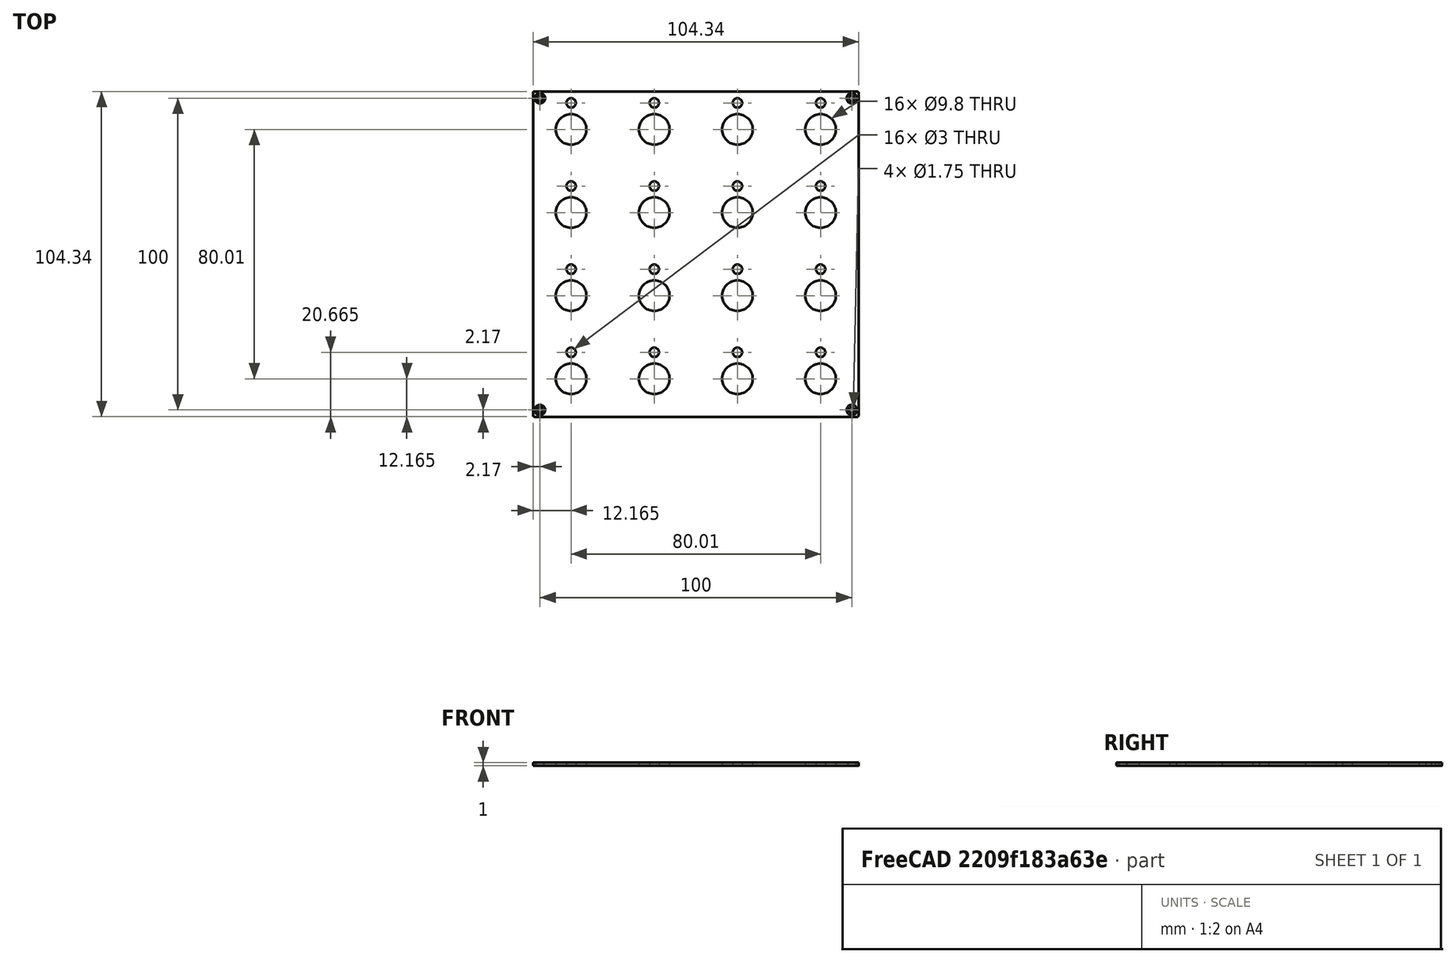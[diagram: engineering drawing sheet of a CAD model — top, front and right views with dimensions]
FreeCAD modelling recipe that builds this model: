
FCSTD DOCUMENT  (FreeCAD 0.21R33771 (Git))
Label: FRONTPANEL-SHEET-BU16
License: All rights reserved
LicenseURL: https://en.wikipedia.org/wiki/All_rights_reserved
objects: TechDraw::DrawViewBalloon×13, TechDraw::DrawViewDimension×8, TechDraw::DrawHatch×7, Sketcher::SketchObject×6, TechDraw::DrawViewPart×5, PartDesign::Hole×3, TechDraw::DrawViewAnnotation×3, TechDraw::DrawSVGTemplate×2, PartDesign::Body×2, TechDraw::DrawPage×2, Spreadsheet::Sheet×1, PartDesign::Pad×1, PartDesign::Pocket×1, PartDesign::FeatureBase×1, TechDraw::DrawComplexSection×1
note: 30 computed .brp shape members not serialized (recipe doc carries the construction recipe); baked Part::Feature solids carry a one-line shape summary decoded from their .brp

FEATURE [TechDraw::DrawSVGTemplate] Template003
  EditableTexts = COLOR=Anodized matte black - RAL code: 9004; CreationDate=2024/05/14; E.G.APPROVED=APPROVED; FC-Scale=1:1; FC-Title=BU16 - frontpanel; IntechStudioLtd.=Intech Studio Ltd.; MATERIAL=Aluminum 5052-H32; REV=03; STANDARD=ISO 2768 - m
  Height = 297
  Orientation = 1
  Template = <userpath>/Desktop/A3_LandscapeTD_MODIFIED.svg
  Width = 420
FEATURE [Spreadsheet::Sheet] Spreadsheet  label="dim"
  cells = A1='panel_length; B1(panel_length)=104.35; A2='panel_thickness; B2(panel_thickness)=1; A3='panel_radius; B3(panel_radius)==(104.35 - 103.6) / 2; A5='corner_drill_dist; B5(corner_drill_dist)=100; A6='corner_drill_dia; B6(corner_drill_dia)=1.75; A7='corner_drill_countersink; B7(corner_drill_countersink)=3.3; A9='undercut_width; B9(undercut_width)=1; A10='undercut_length; B10(undercut_length)=90; A11='undercut_offset; B11(undercut_offset)=1; A12='undercut_depth; B12(undercut_depth)=0.8; A14='ui_raster; B14(ui_raster)=26.67; A16='light_drill_dia; B16(light_drill_dia)=3; D16='old 2.9; A17='light_bore_dia; B17(light_bore_dia)=3.45; C17='check; D17='old 3.30; E17='DEPRICATED; A18='light_bore_depth; B18(light_bore_depth)=0.4; C18='check; D18='old 0.40; E18='DEPRICATED; A20='pot_drill_dia; B20(pot_drill_dia)=9.7; C20='check; D20='old 6.20; A21='pot_led_dist; B21(pot_led_dist)=8.5; B22=0; A23='but_drill_dia; B23(but_drill_dia)=9.8; A24='but_led_dist; B24(but_led_dist)=8.5; A26='fad_cutout_width; B26(fad_cutout_width)=2; C26='check; D26='old 1.50; A27='fad_cutout_length; B27(fad_cutout_length)=36; A28='fad_led_dist; B28(fad_led_dist)=25; A30='enc_drill_dia; B30(enc_drill_dia)=9.7; C30='check; D30='old 6.20; A31='enc_led_dist; B31(enc_led_dist)=8.5; A33='longfad_cutout_width; B33(longfad_cutout_width)=2; A34='longfad_cutout_length; B34(longfad_cutout_length)=66; A36='panel_chamfer; B36(panel_chamfer)=0.2; C36='UPDATE DRAWING
FEATURE [Sketcher::SketchObject] Sketch006
  FullyConstrained = true
  MapMode = 5
  Support = -> [XY_Plane002]
  expr: Constraints[4] = <<dim>>.ui_raster
  expr: Constraints[84] = <<dim>>.but_led_dist
  sketch-geometry (34):
    g0: Circle CenterX=-40.005 CenterY=48.505 CenterZ=0 NormalX=0 NormalY=0 NormalZ=1 AngleXU=0 Radius=2
    g1: Circle CenterX=-13.335 CenterY=48.505 CenterZ=0 NormalX=0 NormalY=0 NormalZ=1 AngleXU=0 Radius=2
    g2: LineSegment StartX=-40.005 StartY=48.505 StartZ=0 EndX=-13.335 EndY=48.505 EndZ=0
    g3: Circle CenterX=13.335 CenterY=48.505 CenterZ=0 NormalX=0 NormalY=0 NormalZ=1 AngleXU=0 Radius=2
    g4: LineSegment StartX=-13.335 StartY=48.505 StartZ=0 EndX=13.335 EndY=48.505 EndZ=0
    g5: Circle CenterX=40.005 CenterY=48.505 CenterZ=0 NormalX=0 NormalY=0 NormalZ=1 AngleXU=0 Radius=2
    g6: LineSegment StartX=13.335 StartY=48.505 StartZ=0 EndX=40.005 EndY=48.505 EndZ=0
    g7: Circle CenterX=-40.005 CenterY=21.835 CenterZ=0 NormalX=0 NormalY=0 NormalZ=1 AngleXU=0 Radius=2
    g8: LineSegment StartX=-40.005 StartY=48.505 StartZ=0 EndX=-40.005 EndY=21.835 EndZ=0
    g9: Circle CenterX=-13.335 CenterY=21.835 CenterZ=0 NormalX=0 NormalY=0 NormalZ=1 AngleXU=0 Radius=2
    g10: LineSegment StartX=-40.005 StartY=21.835 StartZ=0 EndX=-13.335 EndY=21.835 EndZ=0
    g11: Circle CenterX=13.335 CenterY=21.835 CenterZ=0 NormalX=0 NormalY=0 NormalZ=1 AngleXU=0 Radius=2
    g12: LineSegment StartX=-13.335 StartY=21.835 StartZ=0 EndX=13.335 EndY=21.835 EndZ=0
    g13: Circle CenterX=40.005 CenterY=21.835 CenterZ=0 NormalX=0 NormalY=0 NormalZ=1 AngleXU=0 Radius=2
    g14: LineSegment StartX=13.335 StartY=21.835 StartZ=0 EndX=40.005 EndY=21.835 EndZ=0
    g15: Circle CenterX=-40.005 CenterY=-4.835 CenterZ=0 NormalX=0 NormalY=0 NormalZ=1 AngleXU=0 Radius=2
    g16: LineSegment StartX=-40.005 StartY=21.835 StartZ=0 EndX=-40.005 EndY=-4.835 EndZ=0
    g17: Circle CenterX=-13.335 CenterY=-4.835 CenterZ=0 NormalX=0 NormalY=0 NormalZ=1 AngleXU=0 Radius=2
    g18: LineSegment StartX=-40.005 StartY=-4.835 StartZ=0 EndX=-13.335 EndY=-4.835 EndZ=0
    g19: Circle CenterX=13.335 CenterY=-4.835 CenterZ=0 NormalX=0 NormalY=0 NormalZ=1 AngleXU=0 Radius=2
    g20: LineSegment StartX=-13.335 StartY=-4.835 StartZ=0 EndX=13.335 EndY=-4.835 EndZ=0
    g21: Circle CenterX=40.005 CenterY=-4.835 CenterZ=0 NormalX=0 NormalY=0 NormalZ=1 AngleXU=0 Radius=2
    g22: LineSegment StartX=13.335 StartY=-4.835 StartZ=0 EndX=40.005 EndY=-4.835 EndZ=0
    g23: Circle CenterX=-40.005 CenterY=-31.505 CenterZ=0 NormalX=0 NormalY=0 NormalZ=1 AngleXU=0 Radius=2
    g24: LineSegment StartX=-40.005 StartY=-4.835 StartZ=0 EndX=-40.005 EndY=-31.505 EndZ=0
    g25: Circle CenterX=-13.335 CenterY=-31.505 CenterZ=0 NormalX=0 NormalY=0 NormalZ=1 AngleXU=0 Radius=2
    g26: LineSegment StartX=-40.005 StartY=-31.505 StartZ=0 EndX=-13.335 EndY=-31.505 EndZ=0
    g27: Circle CenterX=13.335 CenterY=-31.505 CenterZ=0 NormalX=0 NormalY=0 NormalZ=1 AngleXU=0 Radius=2
    g28: LineSegment StartX=-13.335 StartY=-31.505 StartZ=0 EndX=13.335 EndY=-31.505 EndZ=0
    g29: Circle CenterX=40.005 CenterY=-31.505 CenterZ=0 NormalX=0 NormalY=0 NormalZ=1 AngleXU=0 Radius=2
    g30: LineSegment StartX=13.335 StartY=-31.505 StartZ=0 EndX=40.005 EndY=-31.505 EndZ=0
    g31: LineSegment StartX=-13.335 StartY=21.835 StartZ=0 EndX=-1.8e-15 EndY=8.5 EndZ=0
    g32: LineSegment StartX=-1.8e-15 StartY=8.5 StartZ=0 EndX=13.335 EndY=21.835 EndZ=0
    g33: LineSegment StartX=-1.8e-15 StartY=8.5 StartZ=0 EndX=-13.335 EndY=-4.835 EndZ=0
  constraints (85):
    c: Diameter(g0) = 4
    c: Diameter(g1) = 4
    c: Coincident(g0,g2)
    c: Coincident(g1,g2)
    c: Distance(g2) = 26.67
    c: Angle(g2) = 0
    c: Diameter(g3) = 4
    c: Coincident(g1,g4)
    c: Coincident(g3,g4)
    c: Equal(g2,g4)
    c: Parallel(g4,g2)
    c: Diameter(g5) = 4
    c: Coincident(g3,g6)
    c: Coincident(g5,g6)
    c: Equal(g2,g6)
    c: Parallel(g6,g2)
    c: Diameter(g7) = 4
    c: Coincident(g0,g8)
    c: Coincident(g7,g8)
    c: Equal(g8,g2)
    c: Perpendicular(g8,g2)
    c: Diameter(g9) = 4
    c: Coincident(g7,g10)
    c: Coincident(g9,g10)
    c: Equal(g2,g10)
    c: Parallel(g10,g2)
    c: Diameter(g11) = 4
    c: Coincident(g9,g12)
    c: Coincident(g11,g12)
    c: Equal(g2,g12)
    c: Parallel(g12,g2)
    c: Diameter(g13) = 4
    c: Coincident(g11,g14)
    c: Coincident(g13,g14)
    c: Equal(g2,g14)
    c: Parallel(g14,g2)
    c: Diameter(g15) = 4
    c: Coincident(g7,g16)
    c: Coincident(g15,g16)
    c: Equal(g8,g16)
    c: Perpendicular(g16,g2)
    c: Diameter(g17) = 4
    c: Coincident(g15,g18)
    c: Coincident(g17,g18)
    c: Equal(g2,g18)
    c: Parallel(g18,g2)
    c: Diameter(g19) = 4
    c: Coincident(g17,g20)
    c: Coincident(g19,g20)
    c: Equal(g2,g20)
    c: Parallel(g20,g2)
    c: Diameter(g21) = 4
    c: Coincident(g19,g22)
    c: Coincident(g21,g22)
    c: Equal(g2,g22)
    c: Parallel(g22,g2)
    c: Diameter(g23) = 4
    c: Coincident(g15,g24)
    c: Coincident(g23,g24)
    c: Equal(g8,g24)
    c: Perpendicular(g24,g2)
    c: Diameter(g25) = 4
    c: Coincident(g23,g26)
    c: Coincident(g25,g26)
    c: Equal(g2,g26)
    c: Parallel(g26,g2)
    c: Diameter(g27) = 4
    c: Coincident(g25,g28)
    c: Coincident(g27,g28)
    c: Equal(g2,g28)
    c: Parallel(g28,g2)
    c: Diameter(g29) = 4
    c: Coincident(g27,g30)
    c: Coincident(g29,g30)
    c: Equal(g2,g30)
    c: Parallel(g30,g2)
    c: Coincident(g31,g9)
    c: PointOnObject(g31,g-2)
    c: Coincident(g31,g32)
    c: Coincident(g32,g11)
    c: Coincident(g31,g33)
    c: Coincident(g33,g17)
    c: Equal(g33,g31)
    c: Equal(g31,g32)
    c: DistanceY(g-1,g31) = 8.5
FEATURE [Sketcher::SketchObject] Sketch005
  FullyConstrained = true
  MapMode = 5
  Support = -> [XY_Plane002]
  expr: Constraints[4] = <<dim>>.ui_raster
  sketch-geometry (34):
    g0: Circle CenterX=-40.005 CenterY=40.005 CenterZ=0 NormalX=0 NormalY=0 NormalZ=1 AngleXU=0 Radius=2
    g1: Circle CenterX=-13.335 CenterY=40.005 CenterZ=0 NormalX=0 NormalY=0 NormalZ=1 AngleXU=0 Radius=2
    g2: LineSegment StartX=-40.005 StartY=40.005 StartZ=0 EndX=-13.335 EndY=40.005 EndZ=0
    g3: Circle CenterX=13.335 CenterY=40.005 CenterZ=0 NormalX=0 NormalY=0 NormalZ=1 AngleXU=0 Radius=2
    g4: LineSegment StartX=-13.335 StartY=40.005 StartZ=0 EndX=13.335 EndY=40.005 EndZ=0
    g5: Circle CenterX=40.005 CenterY=40.005 CenterZ=0 NormalX=0 NormalY=0 NormalZ=1 AngleXU=0 Radius=2
    g6: LineSegment StartX=13.335 StartY=40.005 StartZ=0 EndX=40.005 EndY=40.005 EndZ=0
    g7: Circle CenterX=-40.005 CenterY=13.335 CenterZ=0 NormalX=0 NormalY=0 NormalZ=1 AngleXU=0 Radius=2
    g8: LineSegment StartX=-40.005 StartY=40.005 StartZ=0 EndX=-40.005 EndY=13.335 EndZ=0
    g9: Circle CenterX=-13.335 CenterY=13.335 CenterZ=0 NormalX=0 NormalY=0 NormalZ=1 AngleXU=0 Radius=2
    g10: LineSegment StartX=-40.005 StartY=13.335 StartZ=0 EndX=-13.335 EndY=13.335 EndZ=0
    g11: Circle CenterX=13.335 CenterY=13.335 CenterZ=0 NormalX=0 NormalY=0 NormalZ=1 AngleXU=0 Radius=2
    g12: LineSegment StartX=-13.335 StartY=13.335 StartZ=0 EndX=13.335 EndY=13.335 EndZ=0
    g13: Circle CenterX=40.005 CenterY=13.335 CenterZ=0 NormalX=0 NormalY=0 NormalZ=1 AngleXU=0 Radius=2
    g14: LineSegment StartX=13.335 StartY=13.335 StartZ=0 EndX=40.005 EndY=13.335 EndZ=0
    g15: Circle CenterX=-40.005 CenterY=-13.335 CenterZ=0 NormalX=0 NormalY=0 NormalZ=1 AngleXU=0 Radius=2
    g16: LineSegment StartX=-40.005 StartY=13.335 StartZ=0 EndX=-40.005 EndY=-13.335 EndZ=0
    g17: Circle CenterX=-13.335 CenterY=-13.335 CenterZ=0 NormalX=0 NormalY=0 NormalZ=1 AngleXU=0 Radius=2
    g18: LineSegment StartX=-40.005 StartY=-13.335 StartZ=0 EndX=-13.335 EndY=-13.335 EndZ=0
    g19: Circle CenterX=13.335 CenterY=-13.335 CenterZ=0 NormalX=0 NormalY=0 NormalZ=1 AngleXU=0 Radius=2
    g20: LineSegment StartX=-13.335 StartY=-13.335 StartZ=0 EndX=13.335 EndY=-13.335 EndZ=0
    g21: Circle CenterX=40.005 CenterY=-13.335 CenterZ=0 NormalX=0 NormalY=0 NormalZ=1 AngleXU=0 Radius=2
    g22: LineSegment StartX=13.335 StartY=-13.335 StartZ=0 EndX=40.005 EndY=-13.335 EndZ=0
    g23: Circle CenterX=-40.005 CenterY=-40.005 CenterZ=0 NormalX=0 NormalY=0 NormalZ=1 AngleXU=0 Radius=2
    g24: LineSegment StartX=-40.005 StartY=-13.335 StartZ=0 EndX=-40.005 EndY=-40.005 EndZ=0
    g25: Circle CenterX=-13.335 CenterY=-40.005 CenterZ=0 NormalX=0 NormalY=0 NormalZ=1 AngleXU=0 Radius=2
    g26: LineSegment StartX=-40.005 StartY=-40.005 StartZ=0 EndX=-13.335 EndY=-40.005 EndZ=0
    g27: Circle CenterX=13.335 CenterY=-40.005 CenterZ=0 NormalX=0 NormalY=0 NormalZ=1 AngleXU=0 Radius=2
    g28: LineSegment StartX=-13.335 StartY=-40.005 StartZ=0 EndX=13.335 EndY=-40.005 EndZ=0
    g29: Circle CenterX=40.005 CenterY=-40.005 CenterZ=0 NormalX=0 NormalY=0 NormalZ=1 AngleXU=0 Radius=2
    g30: LineSegment StartX=13.335 StartY=-40.005 StartZ=0 EndX=40.005 EndY=-40.005 EndZ=0
    g31: LineSegment StartX=-13.335 StartY=13.335 StartZ=0 EndX=-1.8e-15 EndY=0 EndZ=0
    g32: LineSegment StartX=-1.8e-15 StartY=0 StartZ=0 EndX=13.335 EndY=13.335 EndZ=0
    g33: LineSegment StartX=0 StartY=0 StartZ=0 EndX=-13.335 EndY=-13.335 EndZ=0
  constraints (84):
    c: Diameter(g0) = 4
    c: Diameter(g1) = 4
    c: Coincident(g0,g2)
    c: Coincident(g1,g2)
    c: Distance(g2) = 26.67
    c: Angle(g2) = 0
    c: Diameter(g3) = 4
    c: Coincident(g1,g4)
    c: Coincident(g3,g4)
    c: Equal(g2,g4)
    c: Parallel(g4,g2)
    c: Diameter(g5) = 4
    c: Coincident(g3,g6)
    c: Coincident(g5,g6)
    c: Equal(g2,g6)
    c: Parallel(g6,g2)
    c: Diameter(g7) = 4
    c: Coincident(g0,g8)
    c: Coincident(g7,g8)
    c: Equal(g8,g2)
    c: Perpendicular(g8,g2)
    c: Diameter(g9) = 4
    c: Coincident(g7,g10)
    c: Coincident(g9,g10)
    c: Equal(g2,g10)
    c: Parallel(g10,g2)
    c: Diameter(g11) = 4
    c: Coincident(g9,g12)
    c: Coincident(g11,g12)
    c: Equal(g2,g12)
    c: Parallel(g12,g2)
    c: Diameter(g13) = 4
    c: Coincident(g11,g14)
    c: Coincident(g13,g14)
    c: Equal(g2,g14)
    c: Parallel(g14,g2)
    c: Diameter(g15) = 4
    c: Coincident(g7,g16)
    c: Coincident(g15,g16)
    c: Equal(g8,g16)
    c: Perpendicular(g16,g2)
    c: Diameter(g17) = 4
    c: Coincident(g15,g18)
    c: Coincident(g17,g18)
    c: Equal(g2,g18)
    c: Parallel(g18,g2)
    c: Diameter(g19) = 4
    c: Coincident(g17,g20)
    c: Coincident(g19,g20)
    c: Equal(g2,g20)
    c: Parallel(g20,g2)
    c: Diameter(g21) = 4
    c: Coincident(g19,g22)
    c: Coincident(g21,g22)
    c: Equal(g2,g22)
    c: Parallel(g22,g2)
    c: Diameter(g23) = 4
    c: Coincident(g15,g24)
    c: Coincident(g23,g24)
    c: Equal(g8,g24)
    c: Perpendicular(g24,g2)
    c: Diameter(g25) = 4
    c: Coincident(g23,g26)
    c: Coincident(g25,g26)
    c: Equal(g2,g26)
    c: Parallel(g26,g2)
    c: Diameter(g27) = 4
    c: Coincident(g25,g28)
    c: Coincident(g27,g28)
    c: Equal(g2,g28)
    c: Parallel(g28,g2)
    c: Diameter(g29) = 4
    c: Coincident(g27,g30)
    c: Coincident(g29,g30)
    c: Equal(g2,g30)
    c: Parallel(g30,g2)
    c: Coincident(g31,g9)
    c: Coincident(g31,g-1)
    c: Coincident(g31,g32)
    c: Coincident(g32,g11)
    c: Coincident(g-1,g33)
    c: Coincident(g33,g17)
    c: Equal(g33,g31)
    c: Equal(g31,g32)
FEATURE [Sketcher::SketchObject] Sketch001
  FullyConstrained = true
  MapMode = 5
  Support = -> [XY_Plane]
  expr: Constraints[13] = <<dim>>.corner_drill_dist
  sketch-geometry (9):
    g0: LineSegment StartX=-50 StartY=50 StartZ=0 EndX=-50 EndY=-50 EndZ=0
    g1: LineSegment StartX=-50 StartY=-50 StartZ=0 EndX=50 EndY=-50 EndZ=0
    g2: LineSegment StartX=50 StartY=-50 StartZ=0 EndX=50 EndY=50 EndZ=0
    g3: LineSegment StartX=50 StartY=50 StartZ=0 EndX=-50 EndY=50 EndZ=0
    g4: Circle CenterX=0 CenterY=0 CenterZ=0 NormalX=0 NormalY=0 NormalZ=1 AngleXU=0 Radius=70.7107
    g5: Circle CenterX=-50 CenterY=50 CenterZ=0 NormalX=0 NormalY=0 NormalZ=1 AngleXU=0 Radius=0.5
    g6: Circle CenterX=50 CenterY=50 CenterZ=0 NormalX=0 NormalY=0 NormalZ=1 AngleXU=0 Radius=0.5
    g7: Circle CenterX=50 CenterY=-50 CenterZ=0 NormalX=0 NormalY=0 NormalZ=1 AngleXU=0 Radius=0.5
    g8: Circle CenterX=-50 CenterY=-50 CenterZ=0 NormalX=0 NormalY=0 NormalZ=1 AngleXU=0 Radius=0.5
  constraints (22):
    c: Coincident(g0,g1)
    c: Coincident(g1,g2)
    c: Coincident(g2,g3)
    c: Coincident(g3,g0)
    c: Equal(g0,g1)
    c: Equal(g0,g2)
    c: Equal(g0,g3)
    c: PointOnObject(g0,g4)
    c: PointOnObject(g1,g4)
    c: PointOnObject(g2,g4)
    c: PointOnObject(g3,g4)
    c: Coincident(g4,g-1)
    c: Horizontal(g3)
    c: DistanceX(g3,g3) = 100
    c: Coincident(g5,g0)
    c: Coincident(g6,g2)
    c: Coincident(g7,g1)
    c: Coincident(g8,g0)
    c: Diameter(g8) = 1
    c: Equal(g8,g7)
    c: Equal(g8,g6)
    c: Equal(g8,g5)
FEATURE [Sketcher::SketchObject] Sketch002
  AttachmentOffset = pos=(0,0,-4.8) rot=(0,0,1;0rad)
  FullyConstrained = true
  MapMode = 5
  Placement = pos=(0,0,-4.8) rot=(0,0,1;0rad)
  Support = -> [XY_Plane]
  expr: .AttachmentOffset.Base.z = -<<dim>>.undercut_depth - 4
  expr: Constraints[91] = <<dim>>.undercut_length
  expr: Constraints[92] = <<dim>>.undercut_width
  expr: Constraints[93] = <<dim>>.panel_length / 2 - <<dim>>.undercut_offset - <<dim>>.undercut_width / 2
  sketch-geometry (40):
    g0: LineSegment StartX=-45 StartY=50.175 StartZ=0 EndX=45 EndY=50.175 EndZ=0
    g1: LineSegment StartX=-45 StartY=51.175 StartZ=0 EndX=45 EndY=51.175 EndZ=0
    g2: LineSegment StartX=-50.675 StartY=45 StartZ=0 EndX=0 EndY=0 EndZ=0
    g3: LineSegment StartX=0 StartY=0 StartZ=0 EndX=-50.675 EndY=-45 EndZ=0
    g4: LineSegment StartX=0 StartY=0 StartZ=0 EndX=-45 EndY=50.675 EndZ=0
    g5: LineSegment StartX=45 StartY=50.675 StartZ=0 EndX=0 EndY=0 EndZ=0
    g6: LineSegment StartX=0 StartY=0 StartZ=0 EndX=50.675 EndY=45 EndZ=0
    g7: LineSegment StartX=50.675 StartY=-45 StartZ=0 EndX=0 EndY=0 EndZ=0
    g8: LineSegment StartX=0 StartY=0 StartZ=0 EndX=45 EndY=-50.675 EndZ=0
    g9: LineSegment StartX=0 StartY=0 StartZ=0 EndX=-45 EndY=-50.675 EndZ=0
    g10: ArcOfCircle CenterX=45 CenterY=50.675 CenterZ=0 NormalX=0 NormalY=0 NormalZ=1 AngleXU=0 Radius=0.5 StartAngle=4.71239 EndAngle=6.28319
    g11: ArcOfCircle CenterX=45 CenterY=50.675 CenterZ=0 NormalX=0 NormalY=0 NormalZ=1 AngleXU=0 Radius=0.5 StartAngle=0 EndAngle=1.5708
    g12: LineSegment StartX=45 StartY=50.675 StartZ=0 EndX=45.5 EndY=50.675 EndZ=0
    g13: ArcOfCircle CenterX=-45 CenterY=50.675 CenterZ=0 NormalX=0 NormalY=0 NormalZ=1 AngleXU=0 Radius=0.5 StartAngle=3.14159 EndAngle=4.71239
    g14: ArcOfCircle CenterX=-45 CenterY=50.675 CenterZ=0 NormalX=0 NormalY=0 NormalZ=1 AngleXU=0 Radius=0.5 StartAngle=1.5708 EndAngle=3.14159
    g15: LineSegment StartX=-45.5 StartY=50.675 StartZ=0 EndX=-45 EndY=50.675 EndZ=0
    g16: LineSegment StartX=-45 StartY=-51.175 StartZ=0 EndX=45 EndY=-51.175 EndZ=0
    g17: LineSegment StartX=-45 StartY=-50.175 StartZ=0 EndX=45 EndY=-50.175 EndZ=0
    g18: ArcOfCircle CenterX=45 CenterY=-50.675 CenterZ=0 NormalX=0 NormalY=0 NormalZ=1 AngleXU=0 Radius=0.5 StartAngle=4.71239 EndAngle=6.28319
    g19: ArcOfCircle CenterX=45 CenterY=-50.675 CenterZ=0 NormalX=0 NormalY=0 NormalZ=1 AngleXU=0 Radius=0.5 StartAngle=0 EndAngle=1.5708
    g20: LineSegment StartX=45 StartY=-50.675 StartZ=0 EndX=45.5 EndY=-50.675 EndZ=0
    g21: ArcOfCircle CenterX=-45 CenterY=-50.675 CenterZ=0 NormalX=0 NormalY=0 NormalZ=1 AngleXU=0 Radius=0.5 StartAngle=3.14159 EndAngle=4.71239
    g22: ArcOfCircle CenterX=-45 CenterY=-50.675 CenterZ=0 NormalX=0 NormalY=0 NormalZ=1 AngleXU=0 Radius=0.5 StartAngle=1.5708 EndAngle=3.14159
    g23: LineSegment StartX=-45.5 StartY=-50.675 StartZ=0 EndX=-45 EndY=-50.675 EndZ=0
    g24: LineSegment StartX=51.175 StartY=-45 StartZ=0 EndX=51.175 EndY=45 EndZ=0
    g25: LineSegment StartX=50.175 StartY=-45 StartZ=0 EndX=50.175 EndY=45 EndZ=0
    g26: ArcOfCircle CenterX=50.675 CenterY=45 CenterZ=0 NormalX=0 NormalY=0 NormalZ=1 AngleXU=0 Radius=0.5 StartAngle=3.8e-15 EndAngle=1.5708
    g27: ArcOfCircle CenterX=50.675 CenterY=45 CenterZ=0 NormalX=0 NormalY=0 NormalZ=1 AngleXU=0 Radius=0.5 StartAngle=1.5708 EndAngle=3.14159
    g28: LineSegment StartX=50.675 StartY=45 StartZ=0 EndX=50.675 EndY=45.5 EndZ=0
    g29: ArcOfCircle CenterX=50.675 CenterY=-45 CenterZ=0 NormalX=0 NormalY=0 NormalZ=1 AngleXU=0 Radius=0.5 StartAngle=4.71239 EndAngle=6.28319
    g30: ArcOfCircle CenterX=50.675 CenterY=-45 CenterZ=0 NormalX=0 NormalY=0 NormalZ=1 AngleXU=0 Radius=0.5 StartAngle=3.14159 EndAngle=4.71239
    g31: LineSegment StartX=50.675 StartY=-45.5 StartZ=0 EndX=50.675 EndY=-45 EndZ=0
    g32: LineSegment StartX=-50.175 StartY=-45 StartZ=0 EndX=-50.175 EndY=45 EndZ=0
    g33: LineSegment StartX=-51.175 StartY=-45 StartZ=0 EndX=-51.175 EndY=45 EndZ=0
    g34: ArcOfCircle CenterX=-50.675 CenterY=45 CenterZ=0 NormalX=0 NormalY=0 NormalZ=1 AngleXU=0 Radius=0.5 StartAngle=1.4e-15 EndAngle=1.5708
    g35: ArcOfCircle CenterX=-50.675 CenterY=45 CenterZ=0 NormalX=0 NormalY=0 NormalZ=1 AngleXU=0 Radius=0.5 StartAngle=1.5708 EndAngle=3.14159
    g36: LineSegment StartX=-50.675 StartY=45 StartZ=0 EndX=-50.675 EndY=45.5 EndZ=0
    g37: ArcOfCircle CenterX=-50.675 CenterY=-45 CenterZ=0 NormalX=0 NormalY=0 NormalZ=1 AngleXU=0 Radius=0.5 StartAngle=4.71239 EndAngle=6.28319
    g38: ArcOfCircle CenterX=-50.675 CenterY=-45 CenterZ=0 NormalX=0 NormalY=0 NormalZ=1 AngleXU=0 Radius=0.5 StartAngle=3.14159 EndAngle=4.71239
    g39: LineSegment StartX=-50.675 StartY=-45.5 StartZ=0 EndX=-50.675 EndY=-45 EndZ=0
  constraints (96):
    c: Horizontal(g0)
    c: Coincident(g2,g-1)
    c: Coincident(g2,g3)
    c: Coincident(g-1,g4)
    c: Coincident(g5,g-1)
    c: Coincident(g5,g6)
    c: Coincident(g7,g-1)
    c: Coincident(g7,g8)
    c: Coincident(g-1,g9)
    c: Equal(g5,g6)
    c: Equal(g6,g8)
    c: Equal(g8,g7)
    c: Equal(g7,g9)
    c: Equal(g9,g3)
    c: Equal(g3,g2)
    c: Equal(g2,g4)
    c: Coincident(g10,g5)
    c: Coincident(g11,g10)
    c: Coincident(g11,g10)
    c: Tangent(g11,g1) = 1.5708
    c: Tangent(g10,g0) = -1.5708
    c: Coincident(g12,g10)
    c: Coincident(g12,g10)
    c: Horizontal(g12)
    c: Coincident(g13,g4)
    c: Coincident(g14,g13)
    c: Coincident(g14,g13)
    c: Tangent(g14,g1) = 1.5708
    c: Tangent(g13,g0) = -1.5708
    c: Coincident(g15,g13)
    c: Coincident(g15,g13)
    c: Horizontal(g15)
    c: Horizontal(g1)
    c: Horizontal(g16)
    c: Coincident(g19,g18)
    c: Coincident(g19,g18)
    c: Tangent(g19,g17) = 1.5708
    c: Tangent(g18,g16) = -1.5708
    c: Coincident(g20,g18)
    c: Coincident(g20,g18)
    c: Horizontal(g20)
    c: Coincident(g22,g21)
    c: Coincident(g22,g21)
    c: Tangent(g22,g17) = 1.5708
    c: Tangent(g21,g16) = -1.5708
    c: Coincident(g23,g21)
    c: Coincident(g23,g21)
    c: Horizontal(g23)
    c: Horizontal(g17)
    c: Coincident(g21,g9)
    c: Coincident(g8,g18)
    c: Equal(g22,g14)
    c: Equal(g17,g1)
    c: Coincident(g27,g26)
    c: Coincident(g27,g26)
    c: Tangent(g27,g25) = 1.5708
    c: Tangent(g26,g24) = -1.5708
    c: Coincident(g28,g26)
    c: Coincident(g28,g26)
    c: Coincident(g30,g29)
    c: Coincident(g30,g29)
    c: Tangent(g30,g25) = 1.5708
    c: Tangent(g29,g24) = -1.5708
    c: Coincident(g31,g29)
    c: Coincident(g31,g29)
    c: Vertical(g31)
    c: Vertical(g28)
    c: Vertical(g25)
    c: Vertical(g24)
    c: Coincident(g35,g34)
    c: Coincident(g35,g34)
    c: Tangent(g35,g33) = 1.5708
    c: Tangent(g34,g32) = -1.5708
    c: Coincident(g36,g34)
    c: Coincident(g36,g34)
    c: Coincident(g38,g37)
    c: Coincident(g38,g37)
    c: Tangent(g38,g33) = 1.5708
    c: Tangent(g37,g32) = -1.5708
    c: Coincident(g39,g37)
    c: Coincident(g39,g37)
    c: Vertical(g39)
    c: Vertical(g36)
    c: Vertical(g33)
    c: Vertical(g32)
    c: Coincident(g6,g26)
    c: Coincident(g7,g29)
    c: Equal(g25,g0)
    c: Equal(g11,g27)
    c: Equal(g1,g33)
    c: Equal(g35,g11)
    c: DistanceX(g13,g10) = 90
    c: Diameter(g13) = 1
    c: DistanceY(g-1,g13) = 50.675
    c: Coincident(g2,g34)
    c: Coincident(g3,g37)
FEATURE [Sketcher::SketchObject] Sketch
  FullyConstrained = true
  MapMode = 5
  Support = -> [XY_Plane]
  expr: Constraints[12] = <<dim>>.panel_radius
  expr: Constraints[16] = <<dim>>.panel_length
  sketch-geometry (11):
    g0: LineSegment StartX=-51.8 StartY=52.175 StartZ=0 EndX=51.8 EndY=52.175 EndZ=0
    g1: LineSegment StartX=52.175 StartY=51.8 StartZ=0 EndX=52.175 EndY=-51.8 EndZ=0
    g2: LineSegment StartX=51.8 StartY=-52.175 StartZ=0 EndX=-51.8 EndY=-52.175 EndZ=0
    g3: LineSegment StartX=-52.175 StartY=-51.8 StartZ=0 EndX=-52.175 EndY=51.8 EndZ=0
    g4: ArcOfCircle CenterX=-51.8 CenterY=51.8 CenterZ=0 NormalX=0 NormalY=0 NormalZ=1 AngleXU=0 Radius=0.375 StartAngle=1.5708 EndAngle=3.14159
    g5: ArcOfCircle CenterX=51.8 CenterY=51.8 CenterZ=0 NormalX=0 NormalY=0 NormalZ=1 AngleXU=0 Radius=0.375 StartAngle=8.4e-15 EndAngle=1.5708
    g6: ArcOfCircle CenterX=51.8 CenterY=-51.8 CenterZ=0 NormalX=0 NormalY=0 NormalZ=1 AngleXU=0 Radius=0.375 StartAngle=4.71239 EndAngle=6.28319
    g7: ArcOfCircle CenterX=-51.8 CenterY=-51.8 CenterZ=0 NormalX=0 NormalY=0 NormalZ=1 AngleXU=0 Radius=0.375 StartAngle=3.14159 EndAngle=4.71239
    g8: LineSegment StartX=-51.8 StartY=51.8 StartZ=0 EndX=0 EndY=0 EndZ=0
    g9: LineSegment StartX=0 StartY=0 StartZ=0 EndX=51.8 EndY=51.8 EndZ=0
    g10: LineSegment StartX=0 StartY=0 StartZ=0 EndX=-51.8 EndY=-51.8 EndZ=0
  constraints (26):
    c: Horizontal(g0)
    c: Horizontal(g2)
    c: Vertical(g1)
    c: Vertical(g3)
    c: Tangent(g3,g4) = 1.5708
    c: Tangent(g0,g4) = 1.5708
    c: Tangent(g0,g5) = 1.5708
    c: Tangent(g1,g5) = 1.5708
    c: Tangent(g1,g6) = 1.5708
    c: Tangent(g2,g6) = 1.5708
    c: Tangent(g2,g7) = 1.5708
    c: Tangent(g3,g7) = 1.5708
    c: Radius(g4) = 0.375
    c: Equal(g4,g5)
    c: Equal(g4,g6)
    c: Equal(g4,g7)
    c: DistanceX(g3,g1) = 104.35
    c: Equal(g3,g0)
    c: Coincident(g8,g4)
    c: Coincident(g8,g-1)
    c: Coincident(g8,g9)
    c: Coincident(g9,g5)
    c: Coincident(g-1,g10)
    c: Coincident(g10,g7)
    c: Equal(g10,g8)
    c: Equal(g8,g9)
FEATURE [PartDesign::Pad] Pad  label="panel"
  AllowMultiFace = false
  Direction = (0,0,1)
  Length = 1
  Length2 = 100
  Profile = -> Sketch
  Reversed = true
  Type = 0
  expr: Length = <<dim>>.panel_thickness
FEATURE [PartDesign::Pocket] Pocket
  AllowMultiFace = false
  BaseFeature = -> Pad
  Direction = (0,0,-1)
  Length = 5
  Length2 = 100
  Profile = -> Sketch002
  Type = 1
FEATURE [PartDesign::Hole] Hole
  BaseFeature = -> Pocket
  CustomThreadClearance = 0
  Depth = 298.105
  DepthType = 1
  Diameter = 1.75
  DrillForDepth = false
  DrillPoint = 1
  DrillPointAngle = 118
  HoleCutCountersinkAngle = 90
  HoleCutCustomValues = false
  HoleCutDepth = 0
  HoleCutDiameter = 3.3
  HoleCutType = 2
  ModelThread = false
  Profile = -> Sketch001
  Tapered = false
  TaperedAngle = 90
  ThreadClass = 0
  ThreadDepth = 298.105
  ThreadDepthType = 0
  ThreadDirection = 0
  ThreadFit = 0
  ThreadSize = 0
  ThreadType = 0
  Threaded = false
  UseCustomThreadClearance = false
  expr: Diameter = <<dim>>.corner_drill_dia
  expr: HoleCutDiameter = <<dim>>.corner_drill_countersink
FEATURE [PartDesign::Body] Body  label="Base"
  Group = -> [Sketch,Pad,Sketch001,Sketch002,Pocket,Hole]
  Origin = -> Origin
  Tip = -> Hole
FEATURE [PartDesign::FeatureBase] Clone001
  BaseFeature = -> Body
FEATURE [PartDesign::Hole] Hole003  label="BU16_ButtonHole"
  AllowMultiFace = false
  BaseFeature = -> Clone001
  CustomThreadClearance = 0
  Depth = 25
  DepthType = 1
  Diameter = 9.8
  DrillForDepth = false
  DrillPoint = 0
  DrillPointAngle = 118
  HoleCutCountersinkAngle = 90
  HoleCutCustomValues = false
  HoleCutDepth = 0
  HoleCutDiameter = 0
  HoleCutType = 0
  ModelThread = false
  Profile = -> Sketch005
  Tapered = false
  TaperedAngle = 90
  ThreadClass = 0
  ThreadDepth = 23.5
  ThreadDepthType = 0
  ThreadDirection = 0
  ThreadFit = 0
  ThreadSize = 0
  ThreadType = 0
  Threaded = false
  UseCustomThreadClearance = false
  expr: Diameter = <<dim>>.but_drill_dia
FEATURE [PartDesign::Hole] Hole004  label="BU16_ButtonLight"
  AllowMultiFace = false
  BaseFeature = -> Hole003
  CustomThreadClearance = 0
  Depth = 298.105
  DepthType = 1
  Diameter = 3
  DrillForDepth = false
  DrillPoint = 0
  DrillPointAngle = 118
  HoleCutCountersinkAngle = 90
  HoleCutCustomValues = false
  HoleCutDepth = 0.4
  HoleCutDiameter = 3.45
  HoleCutType = 0
  ModelThread = false
  Profile = -> Sketch006
  Tapered = false
  TaperedAngle = 90
  ThreadClass = 0
  ThreadDepth = 298.105
  ThreadDepthType = 0
  ThreadDirection = 0
  ThreadFit = 0
  ThreadSize = 0
  ThreadType = 0
  Threaded = false
  UseCustomThreadClearance = false
  expr: Diameter = <<dim>>.light_drill_dia
  expr: HoleCutDepth = <<dim>>.light_bore_depth
  expr: HoleCutDiameter = <<dim>>.light_bore_dia
FEATURE [TechDraw::DrawViewAnnotation] Annotation
  Font = osifont
  LineSpace = 100
  LockPosition = false
  MaxWidth = -1
  Rotation = 0
  ScaleType = 0
  Text = 10:1
  TextSize = 4
  TextStyle = 0
  X = 76.4884
  Y = 42.7227
FEATURE [TechDraw::DrawViewAnnotation] Annotation001
  Font = osifont
  LineSpace = 100
  LockPosition = false
  MaxWidth = -1
  Rotation = 0
  ScaleType = 0
  Text = 1:2
  TextSize = 4
  TextStyle = 0
  X = 380.038
  Y = 120.843
FEATURE [Sketcher::SketchObject] Sketch007
  ExternalGeometry = -> [Hole004]
  FullyConstrained = true
  MapMode = 5
  Support = -> [XY_Plane002]
  sketch-geometry (1):
    g0: LineSegment StartX=-53.5 StartY=-50 StartZ=0 EndX=-46.5 EndY=-50 EndZ=0
  constraints (3):
    c: Horizontal(g0)
    c: Symmetric(g0,g0,g-3)
    c: DistanceX(g0,g0) = 7
FEATURE [PartDesign::Body] Body002  label="FRONTPANEL-SHEET-BU16"
  BaseFeature = -> Body
  Group = -> [Clone001,Sketch005,Hole003,Sketch006,Hole004,Sketch007]
  Origin = -> Origin002
  Tip = -> Hole004
FEATURE [TechDraw::DrawViewPart] View  label="View 1"
  CoarseView = false
  Direction = (0,0,1)
  Focus = 100
  HardHidden = false
  IsoCount = 0
  IsoHidden = false
  IsoVisible = false
  LockPosition = false
  Perspective = false
  Rotation = 0
  ScaleType = 2
  ScrubCount = 0
  SeamHidden = false
  SeamVisible = false
  SmoothHidden = false
  SmoothVisible = true
  Source = -> [Body002]
  X = 93.8022
  XDirection = (1,0,0)
  Y = 200.975
FEATURE [TechDraw::DrawViewPart] View002  label="View 2"
  CoarseView = false
  Direction = (-1,0,0)
  Focus = 100
  HardHidden = true
  IsoCount = 0
  IsoHidden = false
  IsoVisible = false
  LockPosition = false
  Perspective = false
  Rotation = 0
  ScaleType = 0
  ScrubCount = 0
  SeamHidden = false
  SeamVisible = false
  SmoothHidden = false
  SmoothVisible = true
  Source = -> [Body002]
  X = 198.963
  XDirection = (0,0,1)
  Y = 203.985
FEATURE [TechDraw::DrawViewPart] View003  label="View 3"
  CoarseView = false
  Direction = (-0.57735,-0.57735,0.57735)
  Focus = 100
  HardHidden = false
  IsoCount = 0
  IsoHidden = false
  IsoVisible = false
  LockPosition = false
  Perspective = false
  Rotation = 0
  Scale = 0.5
  ScaleType = 2
  ScrubCount = 0
  SeamHidden = false
  SeamVisible = false
  SmoothHidden = false
  SmoothVisible = true
  Source = -> [Body002]
  X = 382.784
  XDirection = (-0.707107,5.7735e-07,-0.707107)
  Y = 152.399
FEATURE [TechDraw::DrawViewBalloon] Balloon007
  BubbleShape = 6
  EndType = 6
  EndTypeScale = 1
  KinkLength = -0.1
  LockPosition = false
  OriginX = 0.520628
  OriginY = 38.9805
  Rotation = 0
  ScaleType = 0
  ShapeScale = 1
  SourceView = -> View002
  Text = A
  TextWrapLen = -1
  X = 13.2545
  Y = 38.9634
FEATURE [TechDraw::DrawViewBalloon] Balloon009
  BubbleShape = 6
  EndType = 0
  EndTypeScale = 1
  KinkLength = -0.1
  LockPosition = false
  OriginX = 0.859808
  OriginY = -26.8614
  Rotation = 0
  ScaleType = 0
  ShapeScale = 1
  SourceView = -> View002
  Text = ⏥|0,2
  TextWrapLen = -1
  X = 24.6858
  Y = -26.8434
FEATURE [TechDraw::DrawViewBalloon] Balloon012
  BubbleShape = 6
  EndType = 6
  EndTypeScale = 1
  KinkLength = 0
  LockPosition = false
  OriginX = -18.185
  OriginY = -40.005
  Rotation = 0
  ScaleType = 0
  ShapeScale = 1
  SourceView = -> View
  Text = ⌖|⌀0,15|A|B|C
  TextWrapLen = -1
  X = 6.52725
  Y = -75.2914
FEATURE [TechDraw::DrawViewBalloon] Balloon013
  BubbleShape = 6
  EndType = 6
  EndTypeScale = 1
  KinkLength = 0
  LockPosition = false
  OriginX = -18.185
  OriginY = -40.005
  Rotation = 0
  ScaleType = 0
  ShapeScale = 1
  SourceView = -> View
  Text = ○|0,1
  TextWrapLen = -1
  X = -11.3647
  Y = -85.9016
FEATURE [TechDraw::DrawViewBalloon] Balloon016
  BubbleShape = 6
  EndType = 6
  EndTypeScale = 1
  KinkLength = 0
  LockPosition = false
  OriginX = 11.835
  OriginY = -31.505
  Rotation = 0
  ScaleType = 0
  ShapeScale = 1
  SourceView = -> View
  Text = ⌖|⌀0,15|A|B|C
  TextWrapLen = -1
  X = 75.4647
  Y = -84.3926
FEATURE [TechDraw::DrawViewDimension] Dimension
  AngleOverride = false
  Arbitrary = false
  ArbitraryTolerances = false
  EqualTolerance = true
  ExtensionAngle = 0
  FormatSpec = 16x ⌀%.2w
  FormatSpecOverTolerance = %+.2w
  FormatSpecUnderTolerance = %+.2w
  Inverted = false
  LineAngle = 0
  LockPosition = false
  MeasureType = 1
  OverTolerance = 0.05
  References2D = -> [View]
  Rotation = 0
  ScaleType = 0
  TheoreticalExact = false
  Type = 5
  UnderTolerance = -0.05
  X = 63.7674
  Y = -73.6022
FEATURE [TechDraw::DrawHatch] Hatch  label="HatchF1"
  HatchPattern = C:/Program Files/FreeCAD 0.21/data/Mod/TechDraw/Patterns/solid.svg
  Source = -> View003 [Face1]
FEATURE [TechDraw::DrawViewDimension] Dimension010
  AngleOverride = false
  Arbitrary = false
  ArbitraryTolerances = false
  EqualTolerance = false
  ExtensionAngle = 0
  FormatSpec = %.2w
  FormatSpecOverTolerance = %+.2w
  FormatSpecUnderTolerance = %+.2w
  Inverted = false
  LineAngle = 0
  LockPosition = false
  MeasureType = 1
  OverTolerance = 0
  References2D = -> [View]
  Rotation = 0
  ScaleType = 0
  TheoreticalExact = false
  Type = 2
  UnderTolerance = -0.2
  X = 64.3064
  Y = -0.75489
FEATURE [TechDraw::DrawViewPart] View004
  CoarseView = false
  Direction = (0,0,-1)
  Focus = 100
  HardHidden = true
  IsoCount = 0
  IsoHidden = false
  IsoVisible = false
  LockPosition = false
  Perspective = false
  Rotation = 0
  ScaleType = 0
  ScrubCount = 0
  SeamHidden = false
  SeamVisible = true
  SmoothHidden = false
  SmoothVisible = true
  Source = -> [Body002]
  X = 297.303
  XDirection = (-1,-1e-06,0)
  Y = 200.441
FEATURE [TechDraw::DrawViewDimension] Dimension011
  AngleOverride = false
  Arbitrary = false
  ArbitraryTolerances = false
  EqualTolerance = false
  ExtensionAngle = 0
  FormatSpec = %.2w
  FormatSpecOverTolerance = %+.2w
  FormatSpecUnderTolerance = %+.2w
  Inverted = false
  LineAngle = 0
  LockPosition = false
  MeasureType = 1
  OverTolerance = 0
  References2D = -> [View004]
  Rotation = 0
  ScaleType = 0
  TheoreticalExact = false
  Type = 1
  UnderTolerance = -0.2
  X = -0.499889
  Y = 65.7969
FEATURE [TechDraw::DrawViewBalloon] Balloon022
  BubbleShape = 6
  EndType = 6
  EndTypeScale = 1
  KinkLength = -0.1
  LockPosition = false
  OriginX = -52.2651
  OriginY = 58.6802
  Rotation = 0
  ScaleType = 0
  ShapeScale = 1
  SourceView = -> Dimension011
  Text = B
  TextWrapLen = -1
  X = -62.1979
  Y = 58.6576
FEATURE [TechDraw::DrawViewDimension] Dimension013
  AngleOverride = false
  Arbitrary = false
  ArbitraryTolerances = true
  EqualTolerance = false
  ExtensionAngle = 0
  FormatSpec = 16x ⌀%.2w
  FormatSpecOverTolerance = +0,15
  FormatSpecUnderTolerance = 0
  Inverted = false
  LineAngle = 0
  LockPosition = false
  MeasureType = 1
  OverTolerance = 0
  References2D = -> [View]
  Rotation = 0
  ScaleType = 0
  TheoreticalExact = false
  Type = 5
  UnderTolerance = 0
  X = -11.0501
  Y = -62.5809
FEATURE [TechDraw::DrawComplexSection] ComplexSection  label="Section A - A"
  BaseView = -> View
  Caption = Section A-A
  CoarseView = false
  CutSurfaceDisplay = 2
  CuttingToolWireObject = -> Sketch007
  Direction = (1e-16,-1,0)
  FileGeomPattern = C:/Program Files/FreeCAD 0.21/data/Mod/TechDraw/PAT/FCPAT.pat
  FileHatchPattern = C:/Program Files/FreeCAD 0.21/data/Mod/TechDraw/Patterns/simple.svg
  Focus = 100
  FuseBeforeCut = false
  HardHidden = true
  HatchOffset = (0,0,0)
  HatchRotation = 0
  HatchScale = 1
  IsoCount = 0
  IsoHidden = false
  IsoVisible = false
  LockPosition = false
  NameGeomPattern = Gyémánt bevonatú
  Perspective = false
  ProjectionStrategy = 1
  Rotation = 0
  Scale = 10
  ScaleType = 2
  ScrubCount = 0
  SeamHidden = false
  SeamVisible = true
  SectionDirection = 4
  SectionNormal = (1e-16,-1,0)
  SectionOrigin = (0,0,0)
  SectionSymbol = A
  SmoothHidden = false
  SmoothVisible = true
  Source = -> [Body002]
  TrimAfterCut = false
  X = 79.5678
  XDirection = (1,1e-16,0)
  Y = 64.2074
FEATURE [TechDraw::DrawViewBalloon] Balloon023
  BubbleShape = 1
  EndType = 0
  EndTypeScale = 1
  KinkLength = -0.1
  LockPosition = false
  OriginX = -52.0652
  OriginY = 52.0652
  Rotation = 0
  ScaleType = 0
  ShapeScale = 1
  SourceView = -> View
  Text = 4x R0,38
  TextWrapLen = -1
  X = -70.0132
  Y = 68.6837
FEATURE [TechDraw::DrawViewDimension] Dimension014
  AngleOverride = false
  Arbitrary = false
  ArbitraryTolerances = false
  EqualTolerance = true
  ExtensionAngle = 0
  FormatSpec = %.2w
  FormatSpecOverTolerance = %+.2w
  FormatSpecUnderTolerance = %+.2w
  Inverted = false
  LineAngle = 0
  LockPosition = false
  MeasureType = 1
  OverTolerance = 0
  References2D = -> [ComplexSection]
  Rotation = 0
  ScaleType = 0
  TheoreticalExact = false
  Type = 6
  UnderTolerance = 0
  X = -27.7612
  Y = 28.1448
FEATURE [TechDraw::DrawViewDimension] Dimension015
  AngleOverride = false
  Arbitrary = false
  ArbitraryTolerances = false
  EqualTolerance = true
  ExtensionAngle = 0
  FormatSpec = 4x ⌀%.2w
  FormatSpecOverTolerance = %+.2w
  FormatSpecUnderTolerance = %+.2w
  Inverted = false
  LineAngle = 0
  LockPosition = false
  MeasureType = 1
  OverTolerance = 0
  References2D = -> [ComplexSection]
  Rotation = 0
  ScaleType = 0
  TheoreticalExact = false
  Type = 1
  UnderTolerance = 0
  X = 24.0105
  Y = 22.4679
FEATURE [TechDraw::DrawViewDimension] Dimension016
  AngleOverride = false
  Arbitrary = false
  ArbitraryTolerances = false
  EqualTolerance = true
  ExtensionAngle = 0
  FormatSpec = 4x ⌀%.2w
  FormatSpecOverTolerance = %+.2w
  FormatSpecUnderTolerance = %+.2w
  Inverted = false
  LineAngle = 0
  LockPosition = false
  MeasureType = 1
  OverTolerance = 0.05
  References2D = -> [ComplexSection]
  Rotation = 0
  ScaleType = 0
  TheoreticalExact = false
  Type = 1
  UnderTolerance = -0.05
  X = 52.1239
  Y = -3.38615
FEATURE [TechDraw::DrawViewDimension] Dimension017
  AngleOverride = false
  Arbitrary = false
  ArbitraryTolerances = false
  EqualTolerance = true
  ExtensionAngle = 0
  FormatSpec = (%.2w)
  FormatSpecOverTolerance = %+.2w
  FormatSpecUnderTolerance = %+.2w
  Inverted = false
  LineAngle = 0
  LockPosition = false
  MeasureType = 1
  OverTolerance = 0
  References2D = -> [ComplexSection]
  Rotation = 0
  ScaleType = 0
  TheoreticalExact = false
  Type = 2
  UnderTolerance = 0
  X = -38.4382
  Y = 1.69271
FEATURE [TechDraw::DrawViewBalloon] Balloon024
  BubbleShape = 6
  EndType = 6
  EndTypeScale = 1
  KinkLength = 0
  LockPosition = false
  OriginX = 48.1576
  OriginY = -16.4662
  Rotation = 0
  ScaleType = 0
  ShapeScale = 1
  SourceView = -> Dimension016
  Text = ⌖|⌀0,15|A|B|C
  TextWrapLen = -1
  X = 62.263
  Y = -14.1919
FEATURE [TechDraw::DrawViewAnnotation] Annotation002
  Font = osifont
  LineSpace = 100
  LockPosition = false
  MaxWidth = -1
  Rotation = 0
  ScaleType = 0
  Text = The mid of the datum plane A is preferred to be near | to the lower limit of the flatness tolerance zone. | It can be achieved with an additional bending step. | Aesthetical surfaces colored red on the view | No scratches, burrs or any kind of damage allowed! | Functional surfaces colored blue on the view (all which perpendicular to the aesthetical) | No burrs or other protruding material allowed!
  TextSize = 3
  TextStyle = 0
  X = 296.691
  Y = 101.437
FEATURE [TechDraw::DrawSVGTemplate] Template
  Height = 210
  Orientation = 1
  Template = C:/Program Files/FreeCAD 0.21/data/Mod/TechDraw/Templates/A4_Landscape_blank.svg
  Width = 297
FEATURE [TechDraw::DrawViewPart] View005
  CoarseView = false
  Direction = (0,0,1)
  Focus = 100
  HardHidden = false
  IsoCount = 0
  IsoHidden = false
  IsoVisible = true
  LockPosition = false
  Perspective = false
  Rotation = 0
  ScaleType = 0
  ScrubCount = 0
  SeamHidden = false
  SeamVisible = true
  SmoothHidden = false
  SmoothVisible = true
  Source = -> [Hole004]
  X = 148.5
  XDirection = (1,0,0)
  Y = 105
FEATURE [TechDraw::DrawPage] Page  label="BU16_dxf"
  KeepUpdated = true
  NextBalloonIndex = 1
  ProjectionType = 0
  Template = -> Template
  Views = -> [View005]
FEATURE [TechDraw::DrawViewBalloon] Balloon026
  BubbleShape = 2
  EndType = 6
  EndTypeScale = 1
  KinkLength = 0
  LockPosition = false
  OriginX = -97.7934
  OriginY = -2.76733
  Rotation = 0
  ScaleType = 0
  ShapeScale = 1
  SourceView = -> Annotation002
  Text = 3
  TextWrapLen = -1
  X = -94.5881
  Y = -3.56147
FEATURE [TechDraw::DrawViewBalloon] Balloon027
  BubbleShape = 1
  EndType = 0
  EndTypeScale = 1
  KinkLength = 0
  LockPosition = false
  OriginX = 0.686504
  OriginY = -44.4808
  Rotation = 0
  ScaleType = 0
  ShapeScale = 1
  SourceView = -> View002
  TextWrapLen = -1
  X = 24.7149
  Y = -70.4411
FEATURE [TechDraw::DrawViewBalloon] Balloon028
  BubbleShape = 1
  EndType = 3
  EndTypeScale = 1
  KinkLength = 0
  LockPosition = false
  OriginX = -6.60818
  OriginY = -22.6738
  Rotation = 0
  ScaleType = 0
  ShapeScale = 1
  SourceView = -> View003
  TextWrapLen = -1
  X = -103.988
  Y = -113.663
FEATURE [TechDraw::DrawHatch] Hatch004  label="Hatch004F51"
  HatchPattern = C:/Program Files/FreeCAD 0.21/data/Mod/TechDraw/Patterns/solid.svg
  Source = -> View003 [Face51,Face37,Face48,Face39]
FEATURE [TechDraw::DrawHatch] Hatch005  label="Hatch005F74"
  HatchPattern = C:/Program Files/FreeCAD 0.21/data/Mod/TechDraw/Patterns/solid.svg
  Source = -> View003 [Face74,Face72,Face80,Face84,Face77,Face91,Face49,Face47,Face45,Face38]
FEATURE [TechDraw::DrawHatch] Hatch006  label="Hatch006F50"
  HatchPattern = C:/Program Files/FreeCAD 0.21/data/Mod/TechDraw/Patterns/solid.svg
  Source = -> View003 [Face50,Face40,Face43,Face44,Face73,Face88,Face87,Face86,Face90]
FEATURE [TechDraw::DrawHatch] Hatch007  label="Hatch007F75"
  HatchPattern = C:/Program Files/FreeCAD 0.21/data/Mod/TechDraw/Patterns/solid.svg
  Source = -> View003 [Face75,Edge184,Face36,Face78,Face42,Face46,Face82,Face41,Face83]
FEATURE [TechDraw::DrawHatch] Hatch008  label="Hatch008F76"
  HatchPattern = C:/Program Files/FreeCAD 0.21/data/Mod/TechDraw/Patterns/solid.svg
  Source = -> View003 [Face76,Face79,Face85,Face81,Face89]
FEATURE [TechDraw::DrawHatch] Hatch009  label="Hatch009F3"
  HatchPattern = C:/Program Files/FreeCAD 0.21/data/Mod/TechDraw/Patterns/solid.svg
  Source = -> View003 [Face3,Face2,Face112]
FEATURE [TechDraw::DrawViewBalloon] Balloon
  BubbleShape = 6
  EndType = 6
  EndTypeScale = 1
  KinkLength = -0.1
  LockPosition = false
  OriginX = 72.942
  OriginY = 52.209
  Rotation = 0
  ScaleType = 0
  ShapeScale = 1
  SourceView = -> Balloon012
  Text = C
  TextWrapLen = -1
  X = 73.2859
  Y = 62.7848
FEATURE [TechDraw::DrawViewBalloon] Balloon029
  BubbleShape = 2
  EndType = 6
  EndTypeScale = 1
  KinkLength = 0
  LockPosition = false
  OriginX = 16.1649
  OriginY = -66.3393
  Rotation = 0
  ScaleType = 0
  ShapeScale = 1
  SourceView = -> View
  Text = 3
  TextWrapLen = -1
  X = 19.1544
  Y = -63.5015
FEATURE [TechDraw::DrawPage] Page003  label="BU16_Drawing"
  KeepUpdated = true
  NextBalloonIndex = 39
  ProjectionType = 0
  Template = -> Template003
  Views = -> [View,View002,View003,Balloon007,Balloon009,Balloon012,Balloon013,Balloon016,Dimension,Dimension010,View004,Dimension011,Balloon022,Dimension013,ComplexSection,Balloon023,Dimension014,Dimension015,Dimension016,Dimension017,Balloon024,Annotation002,Balloon026,Balloon027,Balloon028,Annotation,Annotation001,Balloon,Balloon029]
